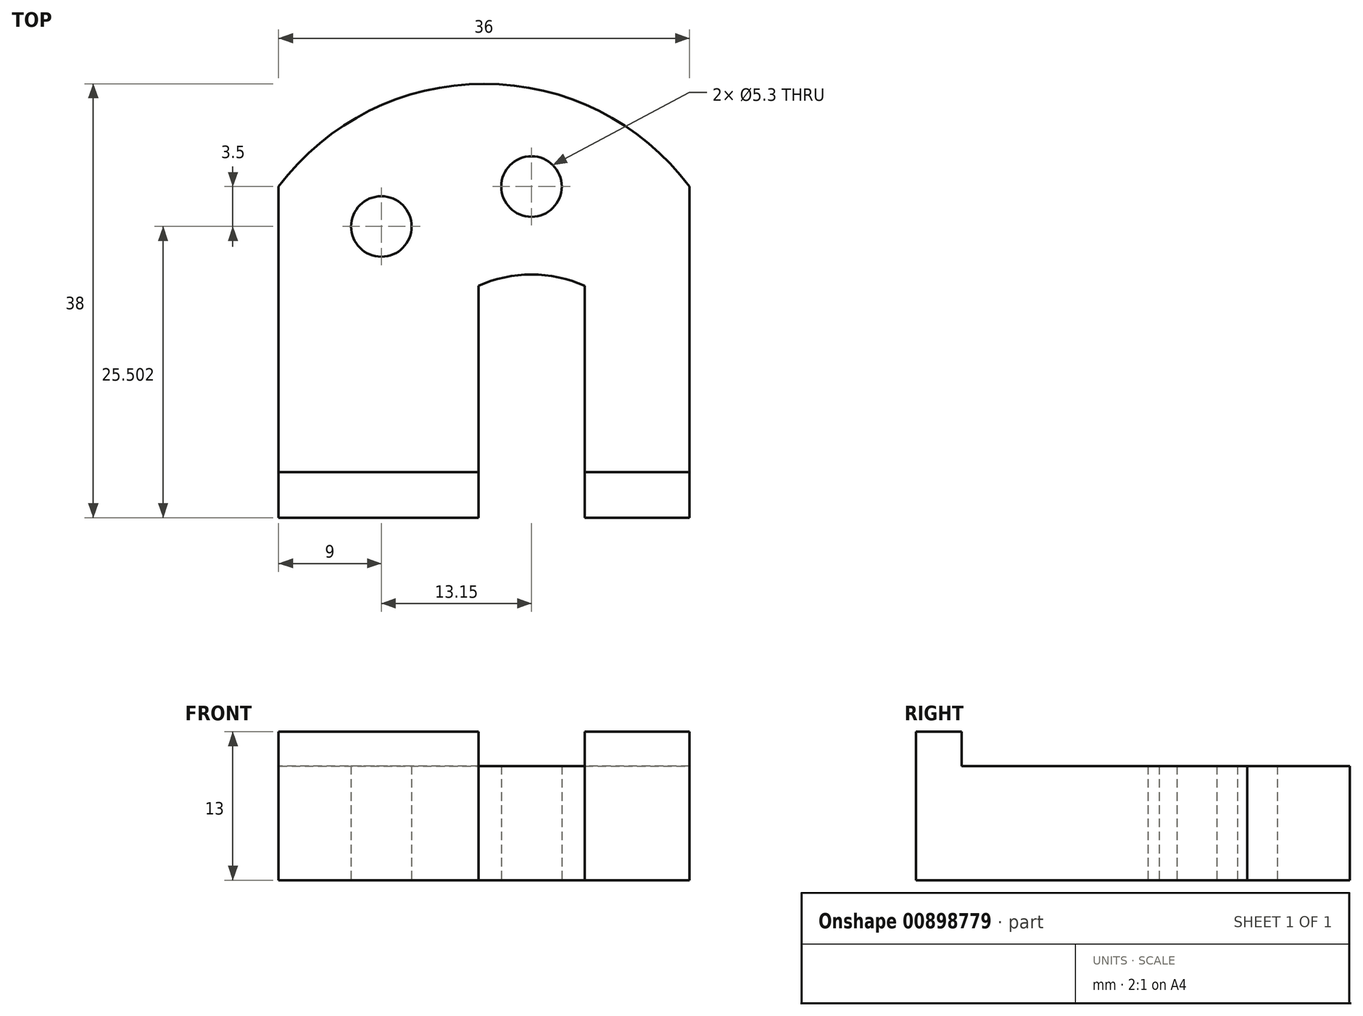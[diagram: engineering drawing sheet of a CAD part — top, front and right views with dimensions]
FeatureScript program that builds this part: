
annotation { "Feature Type Name" : "Feature", "Feature Type Description" : "" }
export const myFeature = defineFeature(function(context is Context, id is Id, definition is map)
    precondition{}
    {
        {
            var Q0;
            Q0=qCreatedBy(makeId("Top.planeOp"),FACE);
            var sketch = newSketch(context, id + "F0", { "sketchPlane" : qUnion([Q0])});
            skLineSegment(sketch, "E0.bottom", {"start": v(-18, 7.88) * mm, "end": v(18, 7.88) * mm, "construction": true});
            skLineSegment(sketch, "E0.top", {"start": v(-18, -17.12) * mm, "end": v(18, -17.12) * mm});
            skLineSegment(sketch, "E0.left", {"start": v(-18, 7.88) * mm, "end": v(-18, -17.12) * mm});
            skLineSegment(sketch, "E0.right", {"start": v(18, 7.88) * mm, "end": v(18, -17.12) * mm});
            skArc(sketch, "E1", {"start": v(18, 7.88) * mm, "mid": v(0, 16.88) * mm, "end": v(-18, 7.88) * mm});
            skCircle(sketch, "E2", {"center": v(-9, 4.38) * mm, "radius": 2.65 * mm});
            skCircle(sketch, "E3", {"center": v(4.15, 7.88) * mm, "radius": 2.65 * mm});
            skLineSegment(sketch, "E4", {"start": v(4.15, 7.88) * mm, "end": v(4.15, -17.12) * mm, "construction": true});
            skArc(sketch, "E5", {"start": v(8.8, -0.82) * mm, "mid": v(4.15, 0.18) * mm, "end": v(-0.5, -0.82) * mm});
            skLineSegment(sketch, "E6", {"start": v(-0.5, -0.82) * mm, "end": v(8.8, -0.82) * mm, "construction": true});
            skLineSegment(sketch, "E7", {"start": v(-0.5, -0.82) * mm, "end": v(-0.5, -17.12) * mm});
            skLineSegment(sketch, "E8", {"start": v(8.8, -0.82) * mm, "end": v(8.8, -17.12) * mm});
            skSolve(sketch);
        }
        {
            var Q0;
            {var subQ1=sQuery(id+"F0.wireOp",EDGE,"E0.left");Q0=makeQuery(id+"F0.imprint","IMPRINT",FACE,{"disambiguationData":[TD([[makeQuery(id+"F0.imprint","IMPRINT",EDGE,{"derivedFrom":subQ1}),1.0]])]});}
            extrude(context, id + "F1", {"entities" : qUnion([Q0]), "depth" : 10 * mm, "offsetDistance" : 25 * mm});
        }
        {
            var Q0;
            {var subQ0=sQuery(id+"F0.wireOp",EDGE,"E0.top");Q0=makeQuery(id+"F1.opExtrude","SWEPT_FACE",FACE,{"disambiguationData":[OSD([subQ0]),TDD([makeQuery(id+"F0.imprint","IMPRINT",EDGE,{"disambiguationData":[TD([[makeQuery(id+"F0.imprint","INTERSECT",VERTEX,{"derivedFrom":[subQ0,sQuery(id+"F0.wireOp",EDGE,"E0.right")]}),1.0]])],"derivedFrom":subQ0})])]});}
            var sketch = newSketch(context, id + "F2", { "sketchPlane" : qUnion([Q0])});
            skLineSegment(sketch, "E9.bottom", {"start": v(-18, 0) * mm, "end": v(18, 0) * mm});
            skLineSegment(sketch, "E9.top", {"start": v(-18, 13) * mm, "end": v(18, 13) * mm});
            skLineSegment(sketch, "E9.left", {"start": v(-18, 0) * mm, "end": v(-18, 13) * mm});
            skLineSegment(sketch, "E9.right", {"start": v(18, 0) * mm, "end": v(18, 13) * mm});
            skLineSegment(sketch, "E10", {"start": v(-0.5, 10) * mm, "end": v(-0.5, 13) * mm});
            skLineSegment(sketch, "E11", {"start": v(8.8, 13) * mm, "end": v(8.8, 10) * mm});
            skSolve(sketch);
        }
        {
            var Q0;
            {var subQ3=sQuery(id+"F0.wireOp",EDGE,"E8");var subQ4=sQuery(id+"F0.wireOp",EDGE,"E0.top");var subQ5=makeQuery(id+"F1.opExtrude","SWEPT_EDGE",EDGE,{"disambiguationData":[OSD([subQ4,subQ3])]});Q0=makeQuery(id+"F2.imprint","IMPRINT",FACE,{"disambiguationData":[TD([[makeQuery(id+"F2.imprint","IMPRINT",EDGE,{"derivedFrom":subQ5}),1.0]])]});}
            var Q1;
            {var subQ3=sQuery(id+"F2.wireOp",EDGE,"E11");Q1=makeQuery(id+"F2.imprint","IMPRINT",FACE,{"disambiguationData":[TD([[makeQuery(id+"F2.imprint","IMPRINT",EDGE,{"derivedFrom":subQ3}),1.0]])]});}
            extrude(context, id + "F3", {"entities" : qUnion([Q0, Q1]), "operationType" : NewBodyOperationType.ADD, "depth" : 4 * mm, "offsetDistance" : 25 * mm});
        }
        {
            var Q0;
            {var subQ0=sQuery(id+"F0.wireOp",EDGE,"E0.top");Q0=makeQuery(id+"F1.opExtrude","SWEPT_FACE",FACE,{"disambiguationData":[OSD([subQ0]),TDD([makeQuery(id+"F0.imprint","IMPRINT",EDGE,{"disambiguationData":[TD([[makeQuery(id+"F0.imprint","INTERSECT",VERTEX,{"derivedFrom":[subQ0,sQuery(id+"F0.wireOp",EDGE,"E0.left")]}),-1.0]])],"derivedFrom":subQ0})])]});}
            var sketch = newSketch(context, id + "F4", { "sketchPlane" : qUnion([Q0])});
            skLineSegment(sketch, "E12.bottom", {"start": v(-18, 0) * mm, "end": v(-0.5, 0) * mm});
            skLineSegment(sketch, "E12.top", {"start": v(-18, 13) * mm, "end": v(-0.5, 13) * mm});
            skLineSegment(sketch, "E12.left", {"start": v(-18, 0) * mm, "end": v(-18, 13) * mm});
            skLineSegment(sketch, "E12.right", {"start": v(-0.5, 0) * mm, "end": v(-0.5, 13) * mm});
            skSolve(sketch);
        }
        {
            var Q0;
            {var subQ0=sQuery(id+"F4.wireOp",EDGE,"E12.bottom");Q0=makeQuery(id+"F4.imprint","IMPRINT",FACE,{"disambiguationData":[TD([[makeQuery(id+"F4.imprint","IMPRINT",EDGE,{"derivedFrom":subQ0}),1.0]])]});}
            var Q1;
            {var subQ0=sQuery(id+"F4.wireOp",EDGE,"E12.top");Q1=makeQuery(id+"F4.imprint","IMPRINT",FACE,{"disambiguationData":[TD([[makeQuery(id+"F4.imprint","IMPRINT",EDGE,{"derivedFrom":subQ0}),-1.0]])]});}
            var Q2;
            Q2=makeQuery(id+"F3.opExtrude","CAP_FACE",FACE,{"disambiguationData":[OSD([sQuery(id+"F0.wireOp",EDGE,"E0.top"),sQuery(id+"F0.wireOp",EDGE,"E8"),sQuery(id+"F2.wireOp",EDGE,"E9.bottom"),sQuery(id+"F2.wireOp",EDGE,"E9.top"),sQuery(id+"F2.wireOp",EDGE,"E9.right"),sQuery(id+"F2.wireOp",EDGE,"E11")])],"isStart":false});
            extrude(context, id + "F5", {"entities" : qUnion([Q0, Q1]), "operationType" : NewBodyOperationType.ADD, "endBound" : BoundingType.UP_TO_SURFACE, "depth" : 25 * mm, "endBoundEntityFace" : qUnion([Q2]), "offsetDistance" : 25 * mm});
        }
    });
